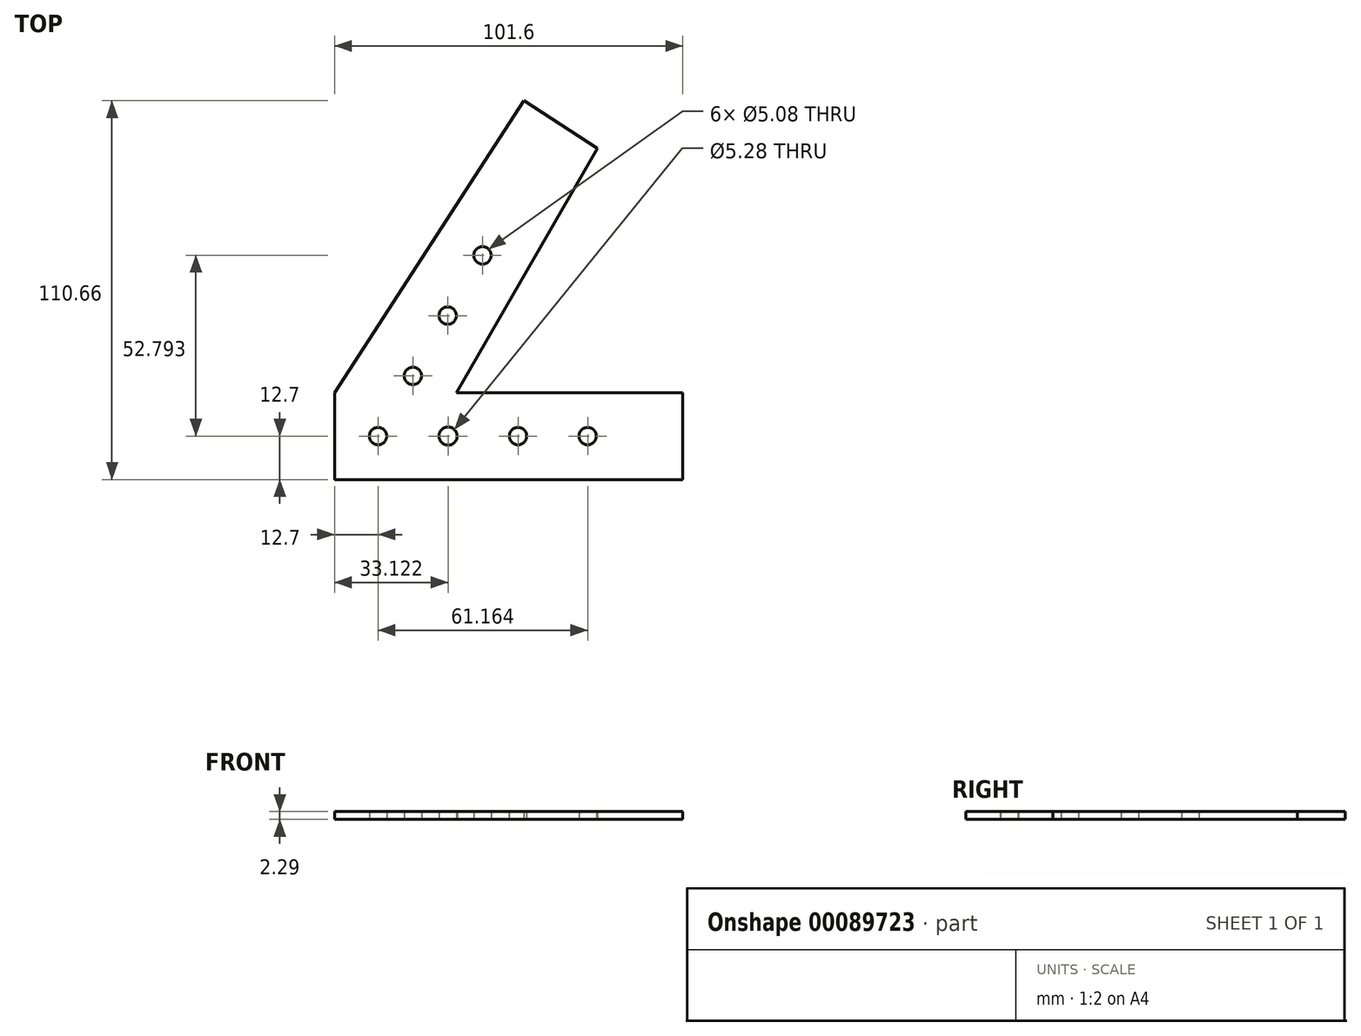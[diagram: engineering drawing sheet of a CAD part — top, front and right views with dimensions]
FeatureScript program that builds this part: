
annotation { "Feature Type Name" : "Feature", "Feature Type Description" : "" }
export const myFeature = defineFeature(function(context is Context, id is Id, definition is map)
    precondition{}
    {
        {
            var Q0;
            Q0=qCreatedBy(makeId("Top.planeOp"),FACE);
            var sketch = newSketch(context, id + "F0", { "sketchPlane" : qUnion([Q0])});
            skLineSegment(sketch, "E0", {"start": v(-44.6, 0) * mm, "end": v(57, 0) * mm});
            skLineSegment(sketch, "E1", {"start": v(-44.6, 0) * mm, "end": v(-44.6, 25.4) * mm});
            skLineSegment(sketch, "E2", {"start": v(-44.6, 25.4) * mm, "end": v(10.66, 110.66) * mm});
            skLineSegment(sketch, "E3", {"start": v(57, 25.4) * mm, "end": v(-9.04, 25.4) * mm});
            skLineSegment(sketch, "E4", {"start": v(-53.74, 12.7) * mm, "end": v(80.3, 12.7) * mm, "construction": true});
            skPoint(sketch, "E4.startSnap0", {"position": v(-44.6, 12.7) * mm});
            skCircle(sketch, "E5", {"center": v(-31.9, 12.7) * mm, "radius": 2.54 * mm});
            skLineSegment(sketch, "E6", {"start": v(-31.9, 12.7) * mm, "end": v(25.86, 112.74) * mm, "construction": true});
            skLineSegment(sketch, "E7", {"start": v(-9.04, 25.4) * mm, "end": v(32.14, 96.73) * mm});
            skLineSegment(sketch, "E8", {"start": v(10.66, 110.66) * mm, "end": v(32.14, 96.73) * mm});
            skLineSegment(sketch, "E9", {"start": v(57, 25.4) * mm, "end": v(57, 0) * mm});
            skCircle(sketch, "E10", {"center": v(-11.48, 12.7) * mm, "radius": 2.64 * mm});
            skCircle(sketch, "E11", {"center": v(8.94, 12.7) * mm, "radius": 2.54 * mm});
            skCircle(sketch, "E12", {"center": v(29.26, 12.7) * mm, "radius": 2.54 * mm});
            skCircle(sketch, "E13", {"center": v(-21.74, 30.3) * mm, "radius": 2.54 * mm});
            skCircle(sketch, "E14", {"center": v(-11.58, 47.9) * mm, "radius": 2.54 * mm});
            skCircle(sketch, "E15", {"center": v(-1.42, 65.5) * mm, "radius": 2.54 * mm});
            skSolve(sketch);
        }
        {
            var Q0;
            Q0=makeQuery(id+"F0.imprint","IMPRINT",FACE,{"disambiguationData":[TD([[makeQuery(id+"F0.imprint","IMPRINT",EDGE,{"derivedFrom":sQuery(id+"F0.wireOp",EDGE,"E0")}),1.0]])]});
            extrude(context, id + "F1", {"entities" : qUnion([Q0]), "depth" : 2.3 * mm});
        }
    });
